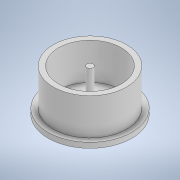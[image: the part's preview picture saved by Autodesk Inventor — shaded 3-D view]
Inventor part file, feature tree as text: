
AUTODESK INVENTOR PART (.ipt)
format: ipt  version: 2022 (Build 260153000, 153)  size: 116,736 bytes
history: native  units: in
note: dims shown in document units (in); Inventor stores cm internally (conversion verified against a paired STEP export)
features: extrude x2, sketch x2
ambient origin geometry x8: Origin, YZ Plane, XZ Plane, XY Plane, X Axis, Y Axis, Z Axis, Center Point
bodies: Solid1 (feature_tree)
feature tree (4):
  extrude  "Extrusion1"  Depth=0.3937in TaperAngle=0.0deg
  extrude  "Extrusion2"  Depth=2.7559in
  sketch  "Sketch1"  dims[d0=6.2992in d1=0.3937in d2=0.0in]
  sketch  "Sketch2"  dims[d3=5.5118in d4=4.7244in d5=0.4724in d6=2.7559in d7=0.0in]
